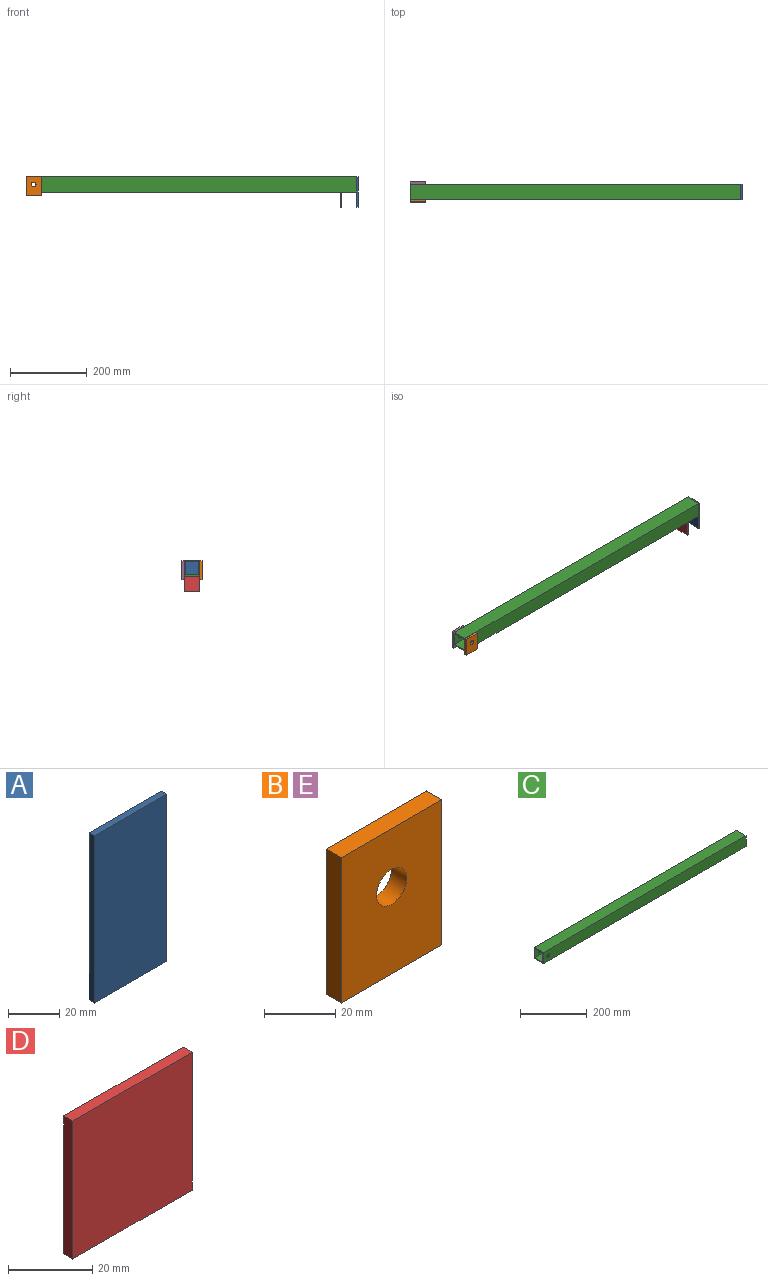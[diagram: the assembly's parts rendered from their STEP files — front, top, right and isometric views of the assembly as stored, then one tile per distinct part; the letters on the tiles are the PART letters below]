
ASSEMBLY  parts=5 mates=4
PART A: 6 faces, bbox 40x3x80 mm
  f0: plane 40x3mm, normal (0,0,-1), area 120mm2, adj f1,f3,f4,f5
  f1: plane 80x3mm, normal (1,0,0), area 240mm2, adj f0,f2,f4,f5
  f2: plane 40x3mm, normal (0,0,1), area 120mm2, adj f1,f3,f4,f5
  f3: plane 80x3mm, normal (-1,0,0), area 240mm2, adj f0,f2,f4,f5
  f4: plane 80x40mm, normal (0,-1,0), area 3200mm2, adj f0,f1,f2,f3
  f5: plane 80x40mm, normal (0,1,0), area 3200mm2, adj f0,f1,f2,f3
PART B: 7 faces, bbox 40x6x50 mm
  f0: plane 40x6mm, normal (0,0,-1), area 240mm2, adj f1,f4,f5,f6
  f1: plane 50x6mm, normal (1,0,0), area 300mm2, adj f0,f2,f5,f6
  f2: plane 40x6mm, normal (0,0,1), area 240mm2, adj f1,f4,f5,f6
  f3: cylinder r=6mm len=12mm, axis (0,1,0), area 226.2mm2, adj f5,f6
  f4: plane 50x6mm, normal (-1,0,0), area 300mm2, adj f0,f2,f5,f6
  f5: plane 50x40mm, normal (0,-1,0), area 1886.9mm2, adj f0,f1,f2,f3,f4
  f6: plane 50x40mm, normal (0,1,0), area 1886.9mm2, adj f0,f1,f2,f3,f4
PART C: 12 faces, bbox 860x40x40 mm
  f0: plane 860x40mm, normal (0,0,-1), area 34400mm2, adj f1,f7,f8,f9
  f1: plane 860x40mm, normal (0,1,0), area 34286.9mm2, adj f0,f2,f8,f9,f11
  f2: plane 860x40mm, normal (0,0,1), area 34400mm2, adj f1,f7,f8,f9
  f3: plane 860x34mm, normal (0,-1,0), area 29126.9mm2, adj f4,f6,f8,f9,f11
  f4: plane 860x34mm, normal (0,0,1), area 29240mm2, adj f3,f5,f8,f9
  f5: plane 860x34mm, normal (0,1,0), area 29126.9mm2, adj f4,f6,f8,f9,f10
  f6: plane 860x34mm, normal (0,0,-1), area 29240mm2, adj f3,f5,f8,f9
  f7: plane 860x40mm, normal (0,-1,0), area 34286.9mm2, adj f0,f2,f8,f9,f10
  f8: plane 40x40mm, normal (1,0,0), area 444mm2, adj f0,f1,f2,f3,f4,f5,f6,f7
  f9: plane 40x40mm, normal (-1,0,0), area 444mm2, adj f0,f1,f2,f3,f4,f5,f6,f7
  f10: cylinder r=6mm len=12mm, axis (0,-1,0), area 113.1mm2, adj f5,f7
  f11: cylinder r=6mm len=12mm, axis (0,-1,0), area 113.1mm2, adj f1,f3
PART D: 6 faces, bbox 40x3x40 mm
  f0: plane 40x3mm, normal (0,0,-1), area 120mm2, adj f1,f3,f4,f5
  f1: plane 40x3mm, normal (1,0,0), area 120mm2, adj f0,f2,f4,f5
  f2: plane 40x3mm, normal (0,0,1), area 120mm2, adj f1,f3,f4,f5
  f3: plane 40x3mm, normal (-1,0,0), area 120mm2, adj f0,f2,f4,f5
  f4: plane 40x40mm, normal (0,-1,0), area 1600mm2, adj f0,f1,f2,f3
  f5: plane 40x40mm, normal (0,1,0), area 1600mm2, adj f0,f1,f2,f3
PART E: same geometry as B
PLACE A rot(axis=(0,0,1),90deg) t=(452.88,12.39,-21.22)mm
PLACE B t=(-387.12,-7.61,-6.22)mm
PLACE C t=(22.88,12.39,-1.22)mm
PLACE D rot(axis=(0,0,1),90deg) t=(410.88,12.39,-41.22)mm
PLACE E t=(-387.12,38.39,-6.22)mm
MATE fastened A.f5 <-> C.f8  axis (-1,0,0) through (452.88,12.39,18.78)mm
MATE fastened D.f2 <-> C.f0  axis (0,0,1) through (410.88,12.39,-21.22)mm
MATE fastened E.f3 <-> C.f10  axis (0,-1,0) through (-387.12,32.39,-1.22)mm
MATE fastened B.f3 <-> C.f10  axis (0,1,0) through (-387.12,-7.61,-1.22)mm
